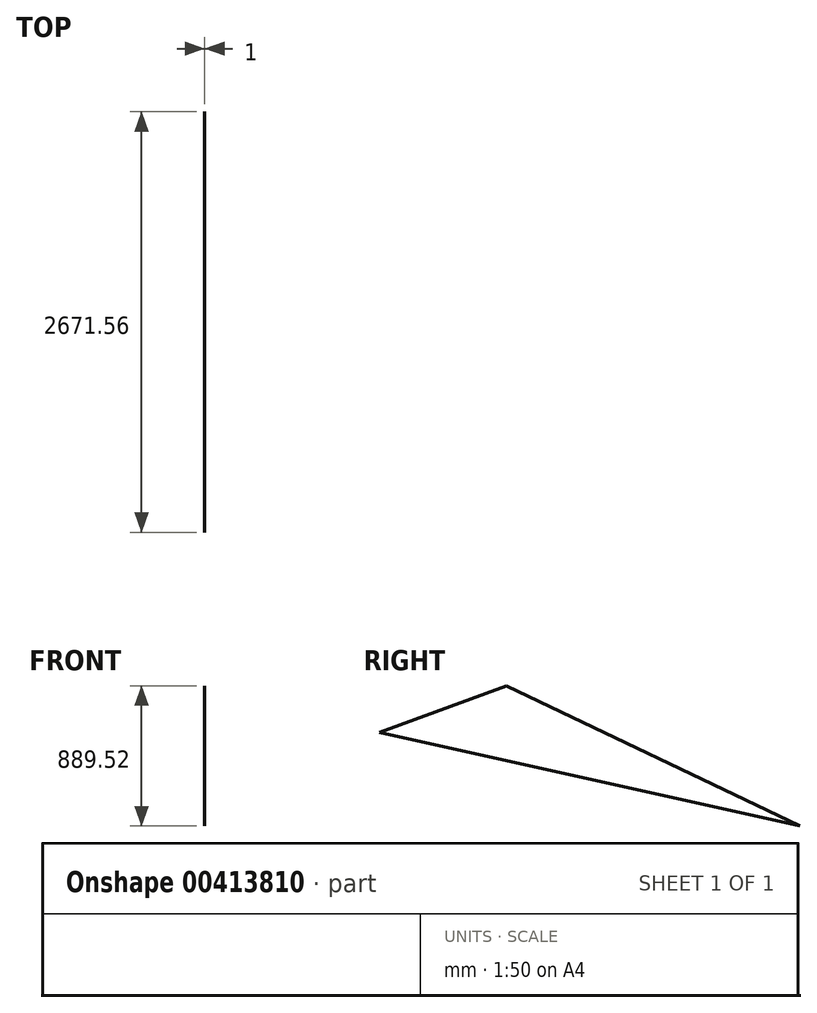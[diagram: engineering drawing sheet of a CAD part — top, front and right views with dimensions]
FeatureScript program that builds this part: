
annotation { "Feature Type Name" : "Feature", "Feature Type Description" : "" }
export const myFeature = defineFeature(function(context is Context, id is Id, definition is map)
    precondition{}
    {
        {
            var Q0;
            Q0=qCreatedBy(makeId("Right.planeOp"),FACE);
            var sketch = newSketch(context, id + "F0", { "sketchPlane" : qUnion([Q0])});
            skLineSegment(sketch, "E0", {"start": v(-400, 0) * mm, "end": v(6100, 0) * mm, "construction": true});
            skLineSegment(sketch, "E1", {"start": v(242.32, 1157.98) * mm, "end": v(1048.12, 1452.58) * mm});
            skLineSegment(sketch, "E2", {"start": v(1048.12, 1452.58) * mm, "end": v(2913.88, 563.06) * mm});
            skSolve(sketch);
        }
        {
            var Q0;
            Q0=sQuery(id+"F0.wireOp",EDGE,"E1");
            var Q1;
            Q1=sQuery(id+"F0.wireOp",VERTEX,"E2.end");
            loft(context, id + "F1", {"bodyType" : ToolBodyType.SURFACE, "wireProfilesArray" : [{ "wireProfileEntities" : qUnion([Q0]) }, { "wireProfileEntities" : qUnion([Q1]) }]});
        }
        {
            var Q0;
            Q0=makeQuery(id+"F1.opLoft","SWEPT_FACE",FACE,{"disambiguationData":[OSD([sQuery(id+"F0.wireOp",VERTEX,"E1.start"),sQuery(id+"F0.wireOp",VERTEX,"E1.end"),sQuery(id+"F0.wireOp",EDGE,"E1")])]});
            extrude(context, id + "F2", {"entities" : qUnion([Q0]), "depth" : mm, "offsetDistance" : 25 * mm});
        }
    });
